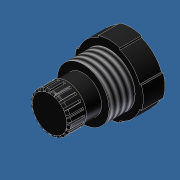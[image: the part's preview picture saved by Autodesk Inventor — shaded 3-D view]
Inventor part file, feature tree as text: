
AUTODESK INVENTOR PART (.ipt)
format: ipt  version: unknown  size: 389,120 bytes
history: native  units: in
note: dims shown in document units (in); Inventor stores cm internally (conversion verified against a paired STEP export)
features: extrude x6, sketch x6, thread x1, pattern_circular x1, fillet x1
ambient origin geometry x8: Origin, YZ Plane, XZ Plane, XY Plane, X Axis, Y Axis, Z Axis, Center Point
bodies: Solid1 (feature_tree)
feature tree (15):
  extrude  "Extrusion1"  Depth=0.5in TaperAngle=0.0deg
  extrude  "Extrusion2"  Depth=0.25in
  extrude  "Extrusion3"  Depth=0.25in
  thread  "Thread1"  [1 undecoded]
  extrude  "Extrusion4"  Depth=0.6in TaperAngle=0.0deg
  extrude  "Extrusion5"  Depth=0.85in
  extrude  "Extrusion6"  Depth=0.9in
  pattern_circular  "Circular Pattern1"  [2 undecoded]
  fillet  "Fillet1"  Radius=0.05in
  sketch  "Sketch1"  dims[d0=1.5in d1=0.5in d2=0.0in]
  sketch  "Sketch2"  dims[d3=0.5in d4=0.25in]
  sketch  "Sketch3"  dims[d5=0.5in d6=0.25in d7=0.5in d8=0.0in]
  sketch  "Sketch4"  dims[d9=1.2in d10=0.6in d11=0.0in]
  sketch  "Sketch5"  dims[d12=1.0in d13=0.0in d14=0.85in]
  sketch  "Sketch6"  dims[d15=0.375in d16=0.0in d17=0.9in d18=0.4in d19=0.0in d20=0.05in d21=0.025in d22=0.05in d23=0.35in d24=0.0in d25=7.874in d26=360.0deg d28=0.05in]
note: 3 required parameter values undecoded (feature->parameter linkage not recoverable at this tier; creation-order binding heuristic only, values carry confidence <= 0.55)
